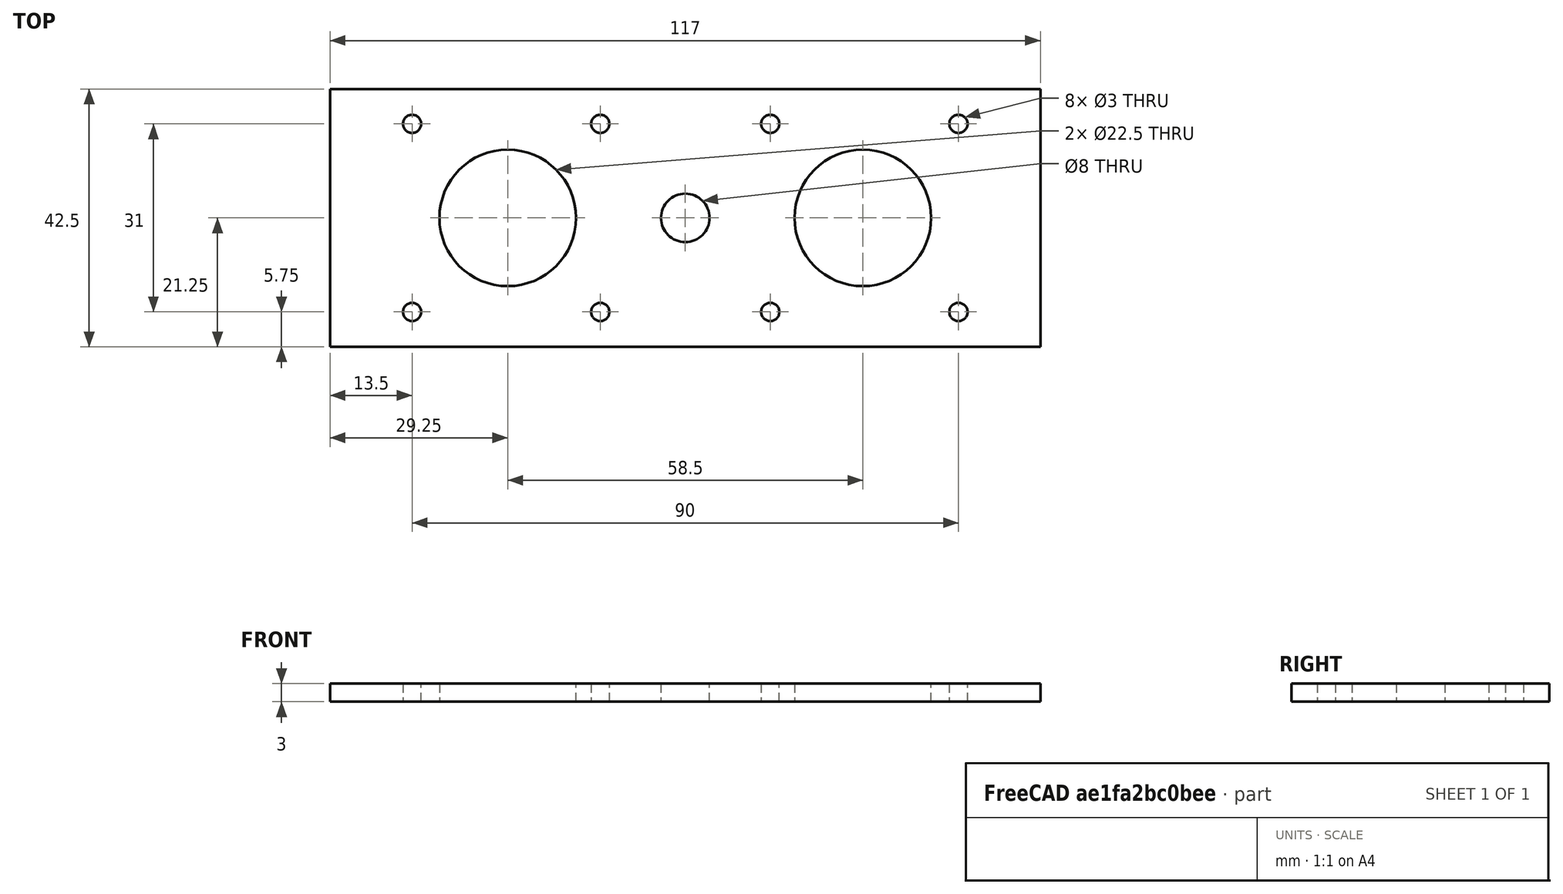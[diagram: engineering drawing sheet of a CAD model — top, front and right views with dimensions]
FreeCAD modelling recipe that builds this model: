
FCSTD DOCUMENT  (FreeCAD 0.16R6712 (Git))
Label: z-axis-motor-mount
License: All rights reserved
LicenseURL: http://en.wikipedia.org/wiki/All_rights_reserved
objects: Sketcher::SketchObject×1, PartDesign::Pad×1
note: 3 computed .brp shape members not serialized (recipe doc carries the construction recipe); baked Part::Feature solids carry a one-line shape summary decoded from their .brp

FEATURE [Sketcher::SketchObject] Sketch
  sketch-geometry (17):
    g0: LineSegment StartX=-58.5 StartY=21.25 StartZ=0 EndX=58.5 EndY=21.25 EndZ=0
    g1: LineSegment StartX=58.5 StartY=21.25 StartZ=0 EndX=58.5 EndY=-21.25 EndZ=0
    g2: LineSegment StartX=58.5 StartY=-21.25 StartZ=0 EndX=-58.5 EndY=-21.25 EndZ=0
    g3: LineSegment StartX=-58.5 StartY=-21.25 StartZ=0 EndX=-58.5 EndY=21.25 EndZ=0
    g4: Circle CenterX=-29.25 CenterY=0 CenterZ=0 NormalX=0 NormalY=0 NormalZ=1 Radius=11.25
    g5: Circle CenterX=29.25 CenterY=0 CenterZ=0 NormalX=0 NormalY=0 NormalZ=1 Radius=11.25
    g6: Circle CenterX=0 CenterY=0 CenterZ=0 NormalX=0 NormalY=0 NormalZ=1 Radius=4
    g7: Circle CenterX=-45 CenterY=15.5 CenterZ=0 NormalX=0 NormalY=0 NormalZ=1 Radius=1.5
    g8: Circle CenterX=-14 CenterY=15.5 CenterZ=0 NormalX=0 NormalY=0 NormalZ=1 Radius=1.5
    g9: Circle CenterX=-14 CenterY=-15.5 CenterZ=0 NormalX=0 NormalY=0 NormalZ=1 Radius=1.5
    g10: Circle CenterX=-45 CenterY=-15.5 CenterZ=0 NormalX=0 NormalY=0 NormalZ=1 Radius=1.5
    g11: Circle CenterX=14 CenterY=15.5 CenterZ=0 NormalX=0 NormalY=0 NormalZ=1 Radius=1.5
    g12: Circle CenterX=45 CenterY=15.5 CenterZ=0 NormalX=0 NormalY=0 NormalZ=1 Radius=1.5
    g13: Circle CenterX=45 CenterY=-15.5 CenterZ=0 NormalX=0 NormalY=0 NormalZ=1 Radius=1.5
    g14: Circle CenterX=14 CenterY=-15.5 CenterZ=0 NormalX=0 NormalY=0 NormalZ=1 Radius=1.5
    g15: LineSegment [constr] StartX=-45 StartY=-15.5 StartZ=0 EndX=-14 EndY=-15.5 EndZ=0
    g16: GeomPoint [constr] X=-29.5 Y=-15.5 Z=0
  constraints (42):
    c: Coincident(g0,g1)
    c: Coincident(g1,g2)
    c: Coincident(g2,g3)
    c: Coincident(g3,g0)
    c: Horizontal(g0)
    c: Horizontal(g2)
    c: Vertical(g1)
    c: Vertical(g3)
    c: DistanceX(g0,g0) = 117
    c: DistanceY(g1,g1) = 42.5
    c: DistanceY(g-1,g0) = 21.25
    c: DistanceX(g-1,g0) = 58.5
    c: PointOnObject(g4,g-1)
    c: PointOnObject(g5,g-1)
    c: Coincident(g6,g-1)
    c: Radius(g6) = 4
    c: Radius(g4) = 11.25
    c: Equal(g4,g5)
    c: Symmetric(g5,g4,g-2)
    c: DistanceX(g-1,g5) = 29.25
    c: Equal(g7,g8)
    c: Equal(g8,g9)
    c: Equal(g9,g10)
    c: Equal(g10,g11)
    c: Equal(g11,g12)
    c: Equal(g12,g13)
    c: Equal(g13,g14)
    c: Radius(g7) = 1.5
    c: Symmetric(g10,g7,g-1)
    c: Symmetric(g12,g13,g-1)
    c: Symmetric(g13,g10,g-2)
    c: Symmetric(g9,g14,g-2)
    c: Symmetric(g9,g8,g-1)
    c: Symmetric(g11,g14,g-1)
    c: DistanceX(g7,g8) = 31
    c: DistanceY(g7,g8) = 0
    c: DistanceY(g10,g7) = 31
    c: Coincident(g15,g10)
    c: Coincident(g15,g9)
    c: PointOnObject(g16,g15)
    c: DistanceX(g10,g16) = 15.5
    c: DistanceX(g16,g-1) = 29.5
FEATURE [PartDesign::Pad] Pad
  Length = 3
  Length2 = 100
  Sketch = -> Sketch
  Type = 0
